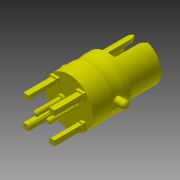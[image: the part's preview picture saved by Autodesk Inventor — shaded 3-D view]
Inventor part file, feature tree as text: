
AUTODESK INVENTOR PART (.ipt)
format: ipt  version: 2014 SP2 (Build 180246200, 246)  size: 288,256 bytes
history: native  units: mm
features: sketch x8, extrude x5, revolve x4
ambient origin geometry x8: Origin, YZ Plane, XZ Plane, XY Plane, X Axis, Y Axis, Z Axis, Center Point
bodies: Solid1 (feature_tree)
feature tree (17):
  revolve  "Revolution1"  [1 undecoded]
  extrude  "Extrusion1"  Depth=2.95mm TaperAngle=0.0deg
  extrude  "Extrusion2"  Depth=0.5mm TaperAngle=0.0deg
  extrude  "Extrusion3"  TaperAngle=360.0deg  [1 undecoded]
  extrude  "Extrusion4"  [1 undecoded]
  extrude  "Extrusion5"  [1 undecoded]
  revolve  "Revolution2"  [1 undecoded]
  revolve  "Revolution3"  [1 undecoded]
  revolve  "Revolution4"  [1 undecoded]
  sketch  "Sketch0"  dims[d0=360.0deg d1=2.0mm d2=0.0mm]
  sketch  "Sketch2"  dims[d3=2.696mm d4=0.0mm d5=2.95mm d6=0.0mm]
  sketch  "Sketch3"  dims[d7=0.5mm d8=0.0mm d9=0.5mm d10=0.0mm]
  sketch  "Sketch4"  dims[d11=360.0deg d12=360.0deg]
  sketch  "Sketch5"  dims[d13=360.0deg]
  sketch  "Sketch6"
  sketch  "Sketch7"
  sketch  "Sketch8"
note: 7 required parameter values undecoded (feature->parameter linkage not recoverable at this tier; creation-order binding heuristic only, values carry confidence <= 0.55)